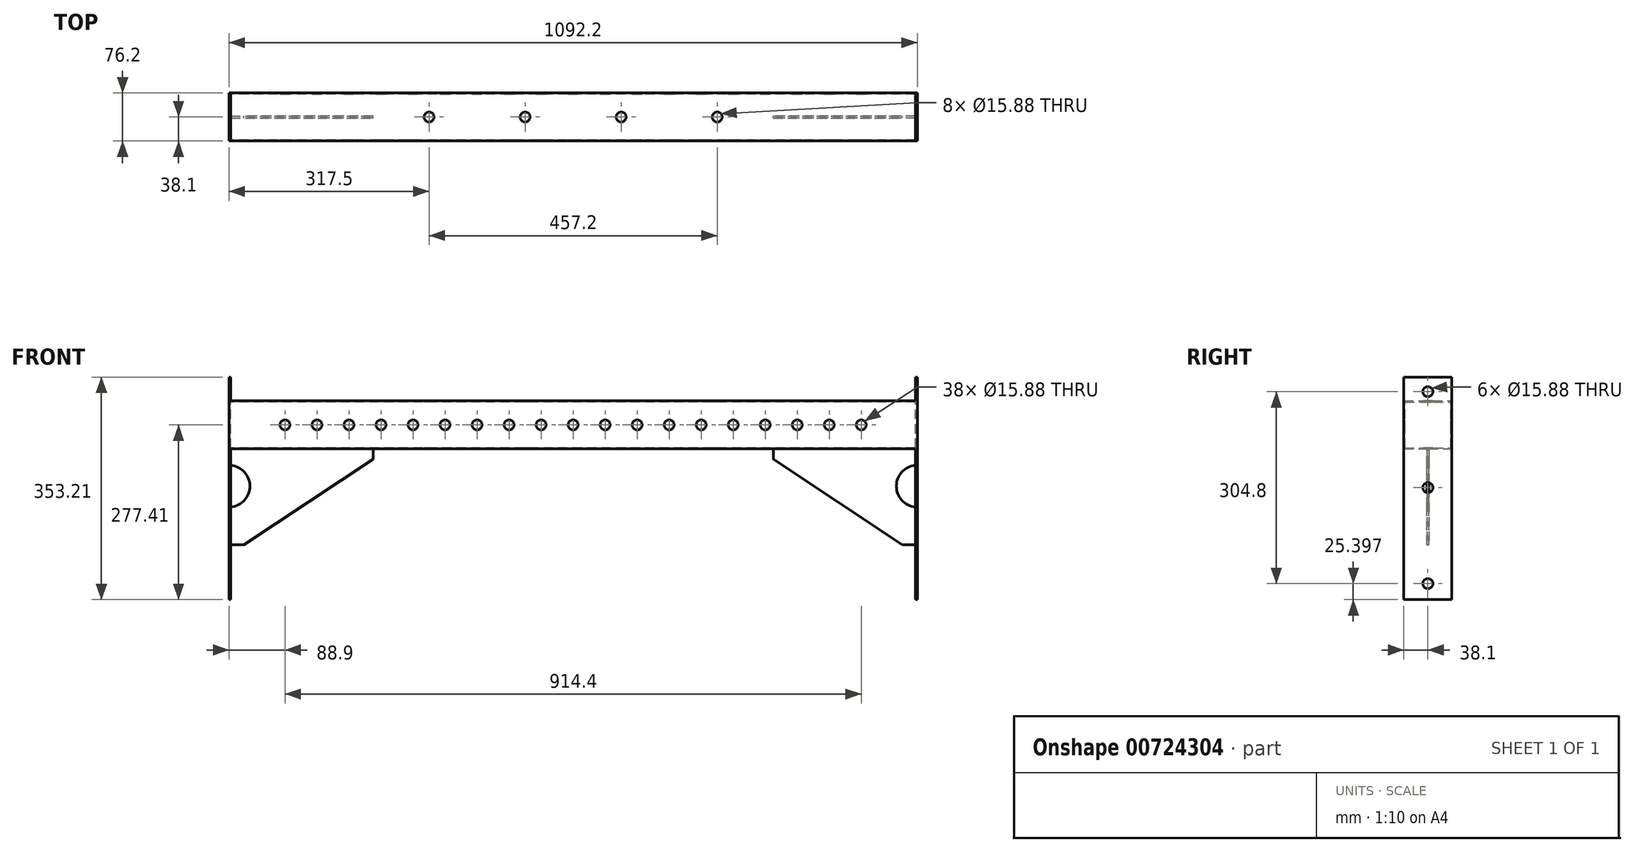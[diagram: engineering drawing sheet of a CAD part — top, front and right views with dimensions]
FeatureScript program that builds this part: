
annotation { "Feature Type Name" : "Feature", "Feature Type Description" : "" }
export const myFeature = defineFeature(function(context is Context, id is Id, definition is map)
    precondition{}
    {
        {
            var Q0;
            Q0=qCreatedBy(makeId("Right.planeOp"),FACE);
            var sketch = newSketch(context, id + "F0", { "sketchPlane" : qUnion([Q0])});
            skLineSegment(sketch, "E0.bottom", {"start": v(-38.1, -38.1) * mm, "end": v(38.1, -38.1) * mm});
            skLineSegment(sketch, "E0.top", {"start": v(-38.1, 38.1) * mm, "end": v(38.1, 38.1) * mm});
            skLineSegment(sketch, "E0.left", {"start": v(-38.1, -38.1) * mm, "end": v(-38.1, 38.1) * mm});
            skLineSegment(sketch, "E0.right", {"start": v(38.1, -38.1) * mm, "end": v(38.1, 38.1) * mm});
            skPoint(sketch, "E0.middle", {"position": v(0, 0) * mm});
            skLineSegment(sketch, "E1.bottom", {"start": v(-36.58, -36.58) * mm, "end": v(36.58, -36.58) * mm});
            skLineSegment(sketch, "E1.top", {"start": v(-36.58, 36.58) * mm, "end": v(36.58, 36.58) * mm});
            skLineSegment(sketch, "E1.left", {"start": v(-36.58, -36.58) * mm, "end": v(-36.58, 36.58) * mm});
            skLineSegment(sketch, "E1.right", {"start": v(36.58, -36.58) * mm, "end": v(36.58, 36.58) * mm});
            skSolve(sketch);
        }
        {
            var Q0;
            Q0=makeQuery(id+"F0.imprint","IMPRINT",FACE,{"disambiguationData":[TD([[makeQuery(id+"F0.imprint","IMPRINT",EDGE,{"derivedFrom":sQuery(id+"F0.wireOp",EDGE,"E0.bottom")}),1.0]])]});
            extrude(context, id + "F1", {"entities" : qUnion([Q0]), "depth" : 1092.2 * mm, "offsetDistance" : 25.4 * mm});
        }
        {
            var Q0;
            Q0=qCreatedBy(makeId("Front.planeOp"),FACE);
            cPlane(context, id + "F2", {"entities" : qUnion([Q0]), "cplaneType" : CPlaneType.OFFSET, "offset" : 76.2 * mm, "width" : 152.4 * mm, "height" : 152.4 * mm});
        }
        {
            var Q0;
            Q0=qCreatedBy(id+"F2.planeOp",FACE);
            var sketch = newSketch(context, id + "F3", { "sketchPlane" : qUnion([Q0])});
            skPoint(sketch, "E2", {"position": v(38.1, 0) * mm});
            skPoint(sketch, "E3.1.0.0", {"position": v(88.9, 0) * mm});
            skPoint(sketch, "E3.2.0.0", {"position": v(139.7, 0) * mm});
            skPoint(sketch, "E3.3.0.0", {"position": v(190.5, 0) * mm});
            skPoint(sketch, "E3.4.0.0", {"position": v(241.3, 0) * mm});
            skPoint(sketch, "E3.5.0.0", {"position": v(292.1, 0) * mm});
            skPoint(sketch, "E3.6.0.0", {"position": v(342.9, 0) * mm});
            skPoint(sketch, "E3.7.0.0", {"position": v(393.7, 0) * mm});
            skPoint(sketch, "E3.8.0.0", {"position": v(444.5, 0) * mm});
            skPoint(sketch, "E3.9.0.0", {"position": v(495.3, 0) * mm});
            skPoint(sketch, "E3.10.0.0", {"position": v(546.1, 0) * mm});
            skPoint(sketch, "E3.11.0.0", {"position": v(596.9, 0) * mm});
            skPoint(sketch, "E3.12.0.0", {"position": v(647.7, 0) * mm});
            skPoint(sketch, "E3.13.0.0", {"position": v(698.5, 0) * mm});
            skPoint(sketch, "E3.14.0.0", {"position": v(749.3, 0) * mm});
            skPoint(sketch, "E3.15.0.0", {"position": v(800.1, 0) * mm});
            skPoint(sketch, "E3.16.0.0", {"position": v(850.9, 0) * mm});
            skPoint(sketch, "E3.17.0.0", {"position": v(901.7, 0) * mm});
            skPoint(sketch, "E3.18.0.0", {"position": v(952.5, 0) * mm});
            skPoint(sketch, "E3.19.0.0", {"position": v(1003.3, 0) * mm});
            skPoint(sketch, "E3.20.0.0", {"position": v(1054.1, 0) * mm});
            skPoint(sketch, "E3.22.0.0", {"position": v(1155.7, 0) * mm});
            skPoint(sketch, "E3.23.0.0", {"position": v(1206.5, 0) * mm});
            skPoint(sketch, "E3.24.0.0", {"position": v(1257.3, 0) * mm});
            skPoint(sketch, "E3.25.0.0", {"position": v(1308.1, 0) * mm});
            skPoint(sketch, "E3.26.0.0", {"position": v(1358.9, 0) * mm});
            skPoint(sketch, "E3.27.0.0", {"position": v(1409.7, 0) * mm});
            skPoint(sketch, "E3.28.0.0", {"position": v(1460.5, 0) * mm});
            skPoint(sketch, "E3.29.0.0", {"position": v(1511.3, 0) * mm});
            skPoint(sketch, "E3.30.0.0", {"position": v(1562.1, 0) * mm});
            skPoint(sketch, "E3.31.0.0", {"position": v(1612.9, 0) * mm});
            skPoint(sketch, "E3.32.0.0", {"position": v(1663.7, 0) * mm});
            skLineSegment(sketch, "E3.direction1", {"start": v(38.1, 0) * mm, "end": v(88.9, 0) * mm, "construction": true});
            skSolve(sketch);
        }
        {
            var Q0;
            Q0=qCreatedBy(makeId("Top.planeOp"),FACE);
            cPlane(context, id + "F4", {"entities" : qUnion([Q0]), "cplaneType" : CPlaneType.OFFSET, "offset" : 76.2 * mm, "width" : 152.4 * mm, "height" : 152.4 * mm});
        }
        {
            var Q0;
            Q0=qCreatedBy(id+"F4.planeOp",FACE);
            var sketch = newSketch(context, id + "F5", { "sketchPlane" : qUnion([Q0])});
            skPoint(sketch, "E4", {"position": v(317.5, 0) * mm});
            skPoint(sketch, "E5.1.0.0", {"position": v(469.9, 0) * mm});
            skPoint(sketch, "E5.2.0.0", {"position": v(622.3, 0) * mm});
            skPoint(sketch, "E5.3.0.0", {"position": v(774.7, 0) * mm});
            skPoint(sketch, "E5.4.0.0", {"position": v(927.1, 0) * mm});
            skPoint(sketch, "E5.5.0.0", {"position": v(1079.5, 0) * mm});
            skPoint(sketch, "E5.6.0.0", {"position": v(1231.9, 0) * mm});
            skPoint(sketch, "E5.7.0.0", {"position": v(1384.3, 0) * mm});
            skLineSegment(sketch, "E5.direction1", {"start": v(317.5, 0) * mm, "end": v(469.9, 0) * mm, "construction": true});
            skSolve(sketch);
        }
        {
            var Q0;
            Q0=sQuery(id+"F3.wireOp",VERTEX,"E3.direction1.start");
            var Q1;
            Q1=sQuery(id+"F3.wireOp",VERTEX,"E3.direction1.end");
            var Q2;
            Q2=sQuery(id+"F3.wireOp",VERTEX,"E3.2.0.0");
            var Q3;
            Q3=sQuery(id+"F3.wireOp",VERTEX,"E3.3.0.0");
            var Q4;
            Q4=sQuery(id+"F3.wireOp",VERTEX,"E3.4.0.0");
            var Q5;
            Q5=sQuery(id+"F3.wireOp",VERTEX,"E3.5.0.0");
            var Q6;
            Q6=sQuery(id+"F3.wireOp",VERTEX,"E3.6.0.0");
            var Q7;
            Q7=sQuery(id+"F3.wireOp",VERTEX,"E3.7.0.0");
            var Q8;
            Q8=sQuery(id+"F3.wireOp",VERTEX,"E3.8.0.0");
            var Q9;
            Q9=sQuery(id+"F3.wireOp",VERTEX,"E3.9.0.0");
            var Q10;
            Q10=sQuery(id+"F3.wireOp",VERTEX,"E3.10.0.0");
            var Q11;
            Q11=sQuery(id+"F3.wireOp",VERTEX,"E3.11.0.0");
            var Q12;
            Q12=sQuery(id+"F3.wireOp",VERTEX,"E3.12.0.0");
            var Q13;
            Q13=sQuery(id+"F3.wireOp",VERTEX,"E3.13.0.0");
            var Q14;
            Q14=sQuery(id+"F3.wireOp",VERTEX,"E3.14.0.0");
            var Q15;
            Q15=sQuery(id+"F3.wireOp",VERTEX,"E3.15.0.0");
            var Q16;
            Q16=sQuery(id+"F3.wireOp",VERTEX,"E3.16.0.0");
            var Q17;
            Q17=sQuery(id+"F3.wireOp",VERTEX,"E3.17.0.0");
            var Q18;
            Q18=sQuery(id+"F3.wireOp",VERTEX,"E3.18.0.0");
            var Q19;
            Q19=sQuery(id+"F3.wireOp",VERTEX,"E3.19.0.0");
            var Q20;
            Q20=sQuery(id+"F5.wireOp",VERTEX,"E4");
            var Q21;
            Q21=sQuery(id+"F5.wireOp",VERTEX,"E5.1.0.0");
            var Q22;
            Q22=sQuery(id+"F5.wireOp",VERTEX,"E5.2.0.0");
            var Q23;
            Q23=sQuery(id+"F5.wireOp",VERTEX,"E5.3.0.0");
            var Q24;
            Q24=sQuery(id+"F5.wireOp",VERTEX,"E5.4.0.0");
            var Q25;
            Q25=makeQuery(id+"F1.opExtrude","SWEPT_BODY",BODY,{"disambiguationData":[OSD([sQuery(id+"F0.wireOp",EDGE,"E0.bottom"),sQuery(id+"F0.wireOp",EDGE,"E0.top"),sQuery(id+"F0.wireOp",EDGE,"E0.left"),sQuery(id+"F0.wireOp",EDGE,"E0.right"),sQuery(id+"F0.wireOp",EDGE,"E1.bottom"),sQuery(id+"F0.wireOp",EDGE,"E1.top"),sQuery(id+"F0.wireOp",EDGE,"E1.left"),sQuery(id+"F0.wireOp",EDGE,"E1.right")])]});
            hole(context, id + "F6", {"style" : HoleStyle.SIMPLE, "endStyle" : HoleEndStyle.THROUGH, "holeDiameter" : 15.88 * mm, "majorDiameter" : 6.35 * mm, "isTappedThrough" : true, "tappedDepth" : 12.7 * mm, "tapClearance" : 3, "locations" : qUnion([Q0, Q1, Q2, Q3, Q4, Q5, Q6, Q7, Q8, Q9, Q10, Q11, Q12, Q13, Q14, Q15, Q16, Q17, Q18, Q19, Q20, Q21, Q22, Q23, Q24]), "scope" : qUnion([Q25])});
        }
        {
            var Q0;
            Q0=qCreatedBy(makeId("Front.planeOp"),FACE);
            var sketch = newSketch(context, id + "F7", { "sketchPlane" : qUnion([Q0])});
            skLineSegment(sketch, "E6.bottom", {"start": v(0, -38.1) * mm, "end": v(228.6, -38.1) * mm});
            skLineSegment(sketch, "E6.left", {"start": v(0, -38.1) * mm, "end": v(0, -190.5) * mm});
            skLineSegment(sketch, "E7", {"start": v(228.6, -54.18) * mm, "end": v(24, -190.5) * mm});
            skLineSegment(sketch, "E8", {"start": v(0, -190.5) * mm, "end": v(24, -190.5) * mm});
            skLineSegment(sketch, "E9", {"start": v(228.6, -38.1) * mm, "end": v(228.6, -54.18) * mm});
            skArc(sketch, "E10", {"start": v(0, -130.38) * mm, "mid": v(33.2, -97.17) * mm, "end": v(0, -63.96) * mm});
            skSolve(sketch);
        }
        {
            var Q0;
            {var subQ3=sQuery(id+"F7.wireOp",EDGE,"E6.bottom");Q0=makeQuery(id+"F7.imprint","IMPRINT",FACE,{"disambiguationData":[TD([[makeQuery(id+"F7.imprint","IMPRINT",EDGE,{"derivedFrom":subQ3}),-1.0]])]});}
            extrude(context, id + "F8", {"entities" : qUnion([Q0]), "operationType" : NewBodyOperationType.ADD, "depth" : 1.52 * mm, "offsetDistance" : 25.4 * mm});
        }
        {
            var Q0;
            {var subQ3=sQuery(id+"F7.wireOp",EDGE,"E6.bottom");Q0=makeQuery(id+"F7.imprint","IMPRINT",FACE,{"disambiguationData":[TD([[makeQuery(id+"F7.imprint","IMPRINT",EDGE,{"derivedFrom":subQ3}),-1.0]])]});}
            extrude(context, id + "F9", {"entities" : qUnion([Q0]), "operationType" : NewBodyOperationType.ADD, "oppositeDirection" : true, "depth" : 1.52 * mm, "offsetDistance" : 25.4 * mm});
        }
        {
            var Q0;
            Q0=qCreatedBy(makeId("Right.planeOp"),FACE);
            var sketch = newSketch(context, id + "F10", { "sketchPlane" : qUnion([Q0])});
            skLineSegment(sketch, "E11.bottom", {"start": v(38.1, 75.8) * mm, "end": v(-38.1, 75.8) * mm});
            skLineSegment(sketch, "E11.top", {"start": v(38.1, -277.41) * mm, "end": v(-38.1, -277.41) * mm});
            skLineSegment(sketch, "E11.left", {"start": v(38.1, 75.8) * mm, "end": v(38.1, -277.41) * mm});
            skLineSegment(sketch, "E11.right", {"start": v(-38.1, 75.8) * mm, "end": v(-38.1, -277.41) * mm});
            skCircle(sketch, "E12", {"center": v(0, -252.01) * mm, "radius": 7.94 * mm});
            skCircle(sketch, "E13", {"center": v(0, -99.61) * mm, "radius": 7.94 * mm});
            skCircle(sketch, "E14", {"center": v(0, 52.79) * mm, "radius": 7.94 * mm});
            skSolve(sketch);
        }
        {
            var Q0;
            Q0=makeQuery(id+"F10.imprint","IMPRINT",FACE,{"disambiguationData":[TD([[makeQuery(id+"F10.imprint","IMPRINT",EDGE,{"derivedFrom":sQuery(id+"F10.wireOp",EDGE,"E11.bottom")}),1.0]])]});
            extrude(context, id + "F11", {"entities" : qUnion([Q0]), "operationType" : NewBodyOperationType.ADD, "depth" : 3.05 * mm, "offsetDistance" : 25.4 * mm});
        }
        {
            var Q0;
            Q0=qCreatedBy(makeId("Right.planeOp"),FACE);
            cPlane(context, id + "F12", {"entities" : qUnion([Q0]), "cplaneType" : CPlaneType.OFFSET, "offset" : 546.1 * mm, "width" : 152.4 * mm, "height" : 152.4 * mm});
        }
        {
            var Q0;
            Q0=makeQuery(id+"F1.opExtrude","SWEPT_BODY",BODY,{"disambiguationData":[OSD([sQuery(id+"F0.wireOp",EDGE,"E0.bottom"),sQuery(id+"F0.wireOp",EDGE,"E0.top"),sQuery(id+"F0.wireOp",EDGE,"E0.left"),sQuery(id+"F0.wireOp",EDGE,"E0.right"),sQuery(id+"F0.wireOp",EDGE,"E1.bottom"),sQuery(id+"F0.wireOp",EDGE,"E1.top"),sQuery(id+"F0.wireOp",EDGE,"E1.left"),sQuery(id+"F0.wireOp",EDGE,"E1.right")])]});
            var Q1;
            Q1=qCreatedBy(id+"F12.planeOp",FACE);
            mirror(context, id + "F13", {"operationType" : NewBodyOperationType.ADD, "entities" : qUnion([Q0]), "mirrorPlane" : qUnion([Q1])});
        }
    });
